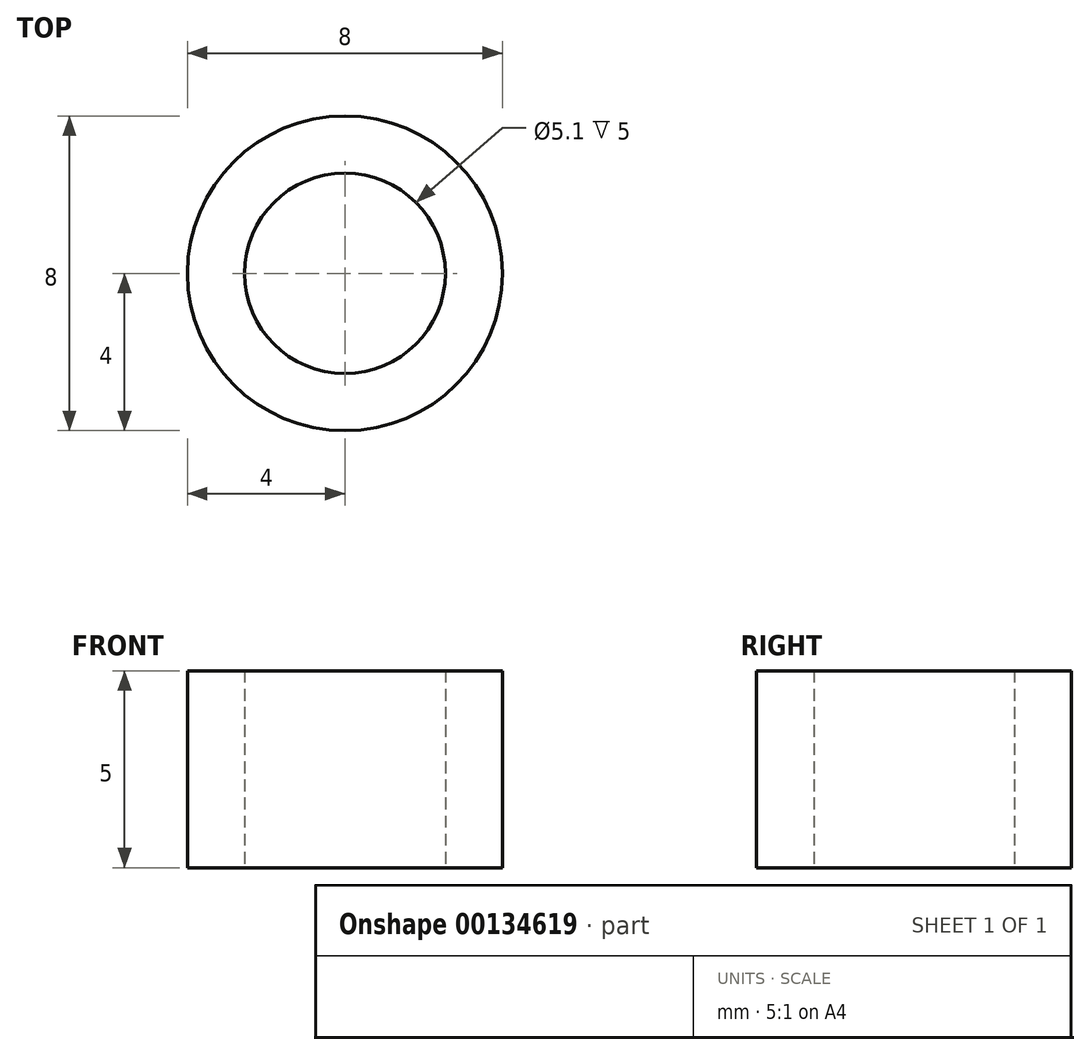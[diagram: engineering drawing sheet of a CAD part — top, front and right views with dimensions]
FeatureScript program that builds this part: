
annotation { "Feature Type Name" : "Feature", "Feature Type Description" : "" }
export const myFeature = defineFeature(function(context is Context, id is Id, definition is map)
    precondition{}
    {
        {
            var Q0;
            Q0=qCreatedBy(makeId("Top.planeOp"),FACE);
            var sketch = newSketch(context, id + "F0", { "sketchPlane" : qUnion([Q0])});
            skCircle(sketch, "E0", {"center": v(0, 0) * mm, "radius": 4 * mm});
            skCircle(sketch, "E1", {"center": v(0, 0) * mm, "radius": 2.55 * mm});
            skSolve(sketch);
        }
        {
            var Q0;
            Q0=makeQuery(id+"F0.imprint","IMPRINT",FACE,{"disambiguationData":[TD([[makeQuery(id+"F0.imprint","IMPRINT",EDGE,{"derivedFrom":sQuery(id+"F0.wireOp",EDGE,"E0")}),1.0]])]});
            extrude(context, id + "F1", {"entities" : qUnion([Q0]), "depth" : 5 * mm});
        }
    });
